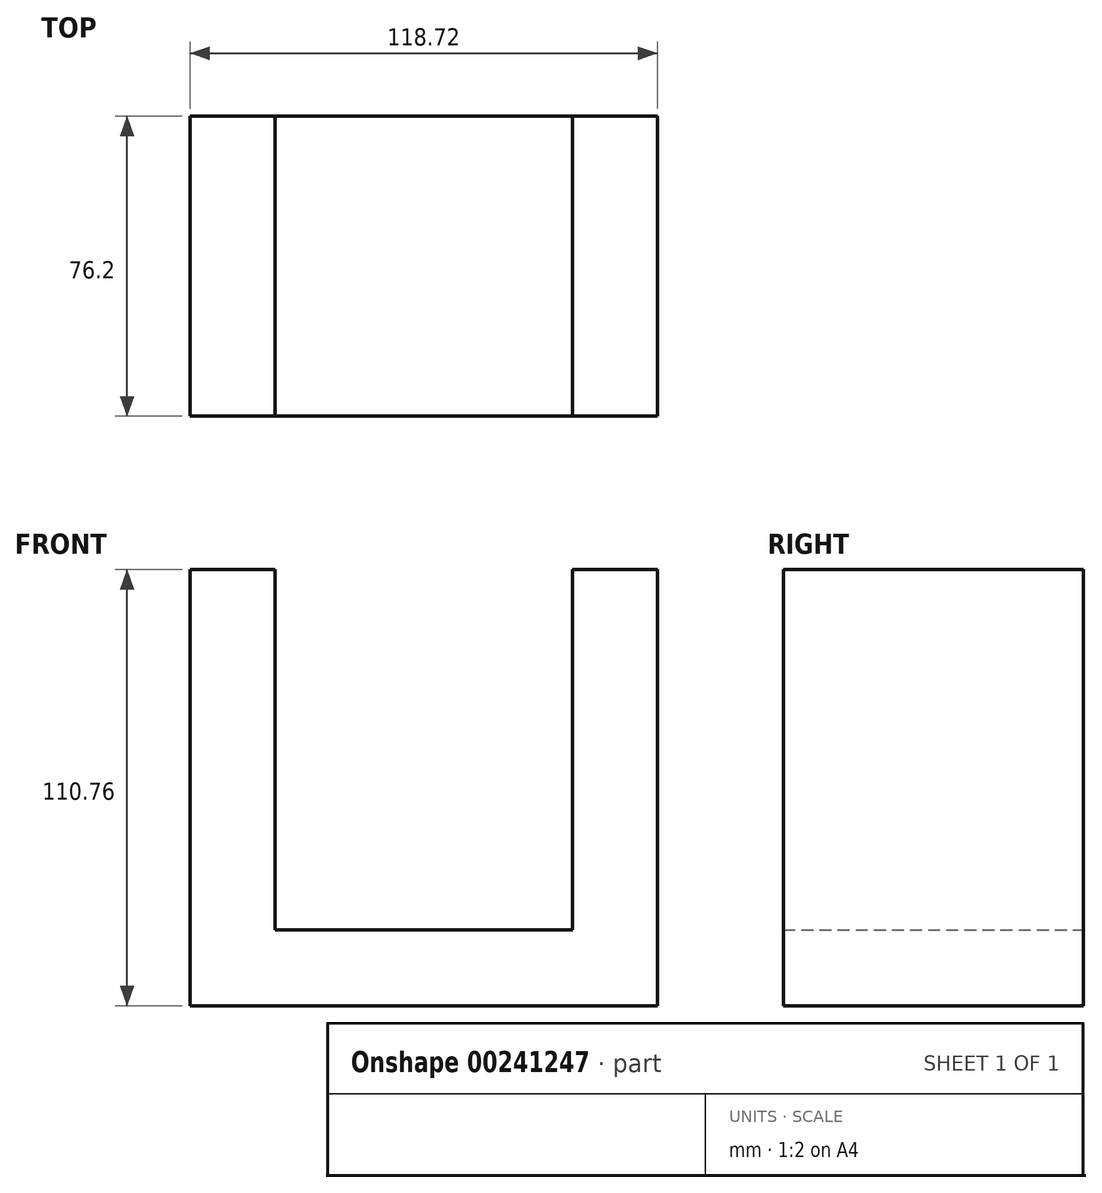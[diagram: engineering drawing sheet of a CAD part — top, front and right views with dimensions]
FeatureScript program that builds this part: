
annotation { "Feature Type Name" : "Feature", "Feature Type Description" : "" }
export const myFeature = defineFeature(function(context is Context, id is Id, definition is map)
    precondition{}
    {
        {
            var Q0;
            Q0=qCreatedBy(makeId("Front.planeOp"),FACE);
            var sketch = newSketch(context, id + "F0", { "sketchPlane" : qUnion([Q0])});
            skLineSegment(sketch, "E0", {"start": v(-57.97, -56.06) * mm, "end": v(-57.97, 54.7) * mm});
            skLineSegment(sketch, "E1", {"start": v(-57.97, -56.06) * mm, "end": v(60.75, -56.06) * mm});
            skLineSegment(sketch, "E2", {"start": v(60.75, -56.06) * mm, "end": v(60.75, 54.7) * mm});
            skLineSegment(sketch, "E3", {"start": v(60.75, 54.7) * mm, "end": v(39.19, 54.7) * mm});
            skLineSegment(sketch, "E4", {"start": v(39.19, 54.7) * mm, "end": v(39.19, -36.74) * mm});
            skLineSegment(sketch, "E5", {"start": v(39.19, -36.74) * mm, "end": v(-36.4, -36.74) * mm});
            skLineSegment(sketch, "E6", {"start": v(-36.4, -36.74) * mm, "end": v(-36.4, 54.7) * mm});
            skLineSegment(sketch, "E7", {"start": v(-36.4, 54.7) * mm, "end": v(-57.97, 54.7) * mm});
            skSolve(sketch);
        }
        {
            var Q0;
            Q0=makeQuery(id+"F0.imprint","IMPRINT",FACE,{"disambiguationData":[TD([[makeQuery(id+"F0.imprint","IMPRINT",EDGE,{"derivedFrom":sQuery(id+"F0.wireOp",EDGE,"E0")}),-1.0]])]});
            extrude(context, id + "F1", {"entities" : qUnion([Q0]), "depth" : 76.2 * mm});
        }
    });
